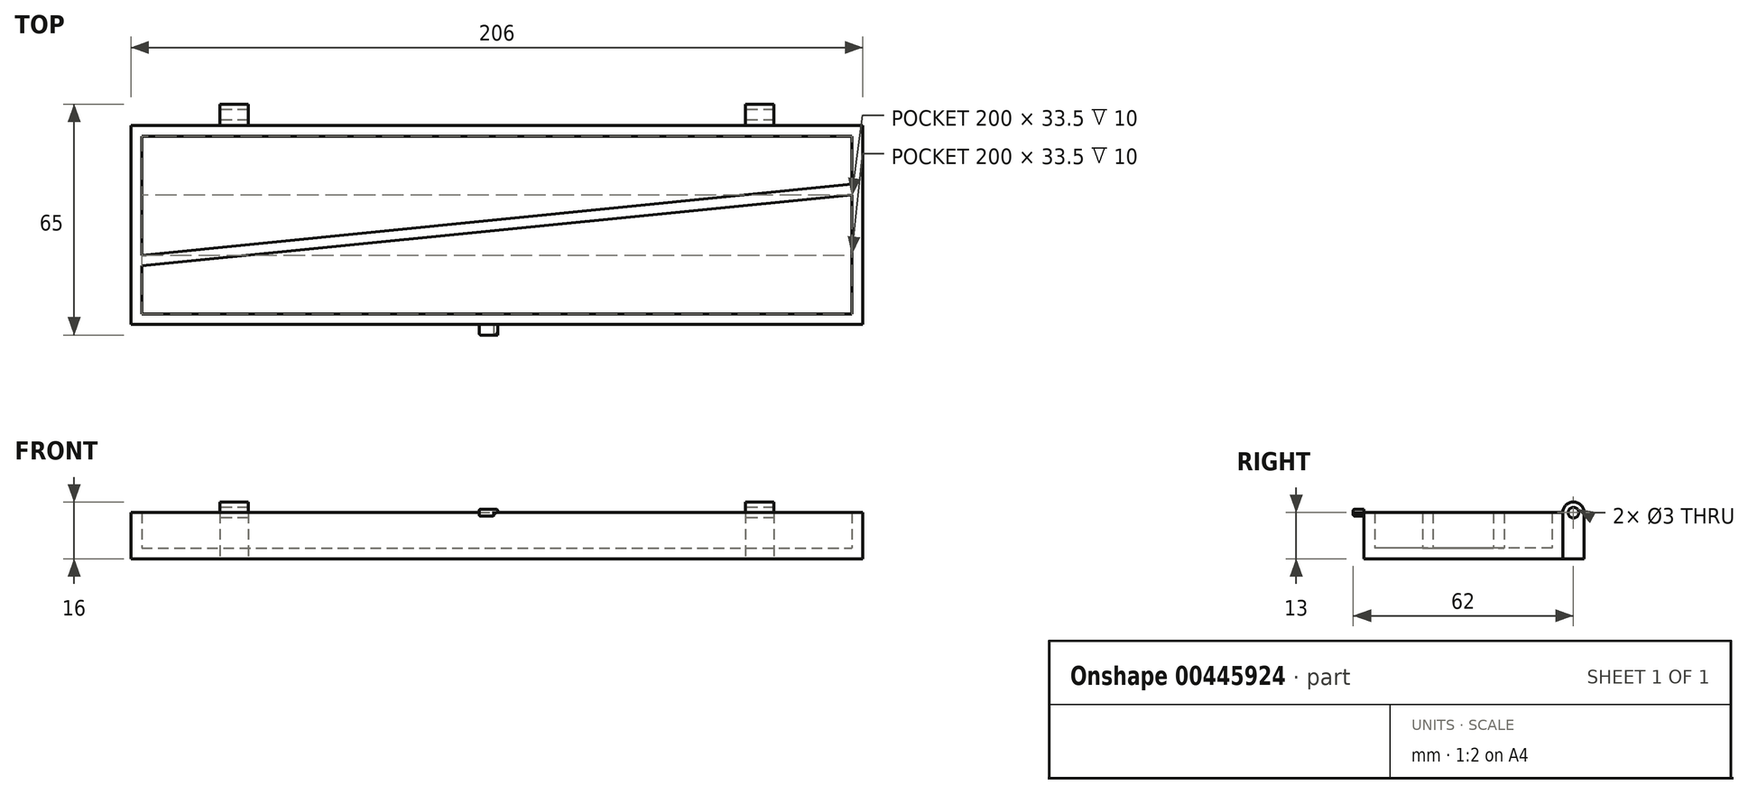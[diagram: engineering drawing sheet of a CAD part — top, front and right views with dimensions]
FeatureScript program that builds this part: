
annotation { "Feature Type Name" : "Feature", "Feature Type Description" : "" }
export const myFeature = defineFeature(function(context is Context, id is Id, definition is map)
    precondition{}
    {
        {
            var Q0;
            Q0=qCreatedBy(makeId("Top.planeOp"),FACE);
            var sketch = newSketch(context, id + "F0", { "sketchPlane" : qUnion([Q0])});
            skLineSegment(sketch, "E0.bottom", {"start": v(-103, 28) * mm, "end": v(103, 28) * mm});
            skLineSegment(sketch, "E0.top", {"start": v(-103, -28) * mm, "end": v(103, -28) * mm});
            skLineSegment(sketch, "E0.left", {"start": v(-103, 28) * mm, "end": v(-103, -28) * mm});
            skLineSegment(sketch, "E0.right", {"start": v(103, 28) * mm, "end": v(103, -28) * mm});
            skSolve(sketch);
        }
        {
            var Q0;
            Q0 = qSketchRegion(id + "F0", true);
            extrude(context, id + "F1", {"entities" : qUnion([Q0]), "depth" : 13 * mm});
        }
        {
            var Q0;
            Q0=makeQuery(id+"F1.opExtrude","CAP_FACE",FACE,{"disambiguationData":[OSD([sQuery(id+"F0.wireOp",EDGE,"E0.bottom"),sQuery(id+"F0.wireOp",EDGE,"E0.top"),sQuery(id+"F0.wireOp",EDGE,"E0.left"),sQuery(id+"F0.wireOp",EDGE,"E0.right")])],"isStart":false});
            shell(context, id + "F2", {"entities" : qUnion([Q0]), "thickness" : 3 * mm});
        }
        {
            var Q0;
            Q0=makeQuery(id+"F2.opShell","OFFSET_FACE",FACE,{"disambiguationData":[OSD([sQuery(id+"F0.wireOp",EDGE,"E0.bottom"),sQuery(id+"F0.wireOp",EDGE,"E0.top"),sQuery(id+"F0.wireOp",EDGE,"E0.left"),sQuery(id+"F0.wireOp",EDGE,"E0.right")])]});
            var sketch = newSketch(context, id + "F3", { "sketchPlane" : qUnion([Q0])});
            skLineSegment(sketch, "E1", {"start": v(-100, -8.5) * mm, "end": v(100, 11.5) * mm});
            skLineSegment(sketch, "E2", {"start": v(-100, -11.5) * mm, "end": v(100, 8.5) * mm});
            skLineSegment(sketch, "E3", {"start": v(-100, -11.5) * mm, "end": v(-100, -8.5) * mm});
            skLineSegment(sketch, "E4", {"start": v(100, 8.5) * mm, "end": v(100, 11.5) * mm});
            skSolve(sketch);
        }
        {
            var Q0;
            Q0 = qSketchRegion(id + "F3", true);
            extrude(context, id + "F4", {"entities" : qUnion([Q0]), "operationType" : NewBodyOperationType.ADD, "depth" : 10 * mm});
        }
        {
            var Q0;
            Q0=makeQuery(id+"F1.opExtrude","SWEPT_FACE",FACE,{"disambiguationData":[OSD([sQuery(id+"F0.wireOp",EDGE,"E0.bottom")])]});
            var sketch = newSketch(context, id + "F5", { "sketchPlane" : qUnion([Q0])});
            skLineSegment(sketch, "E5.bottom", {"start": v(-78, 13) * mm, "end": v(-70, 13) * mm});
            skLineSegment(sketch, "E5.top", {"start": v(-78, 0) * mm, "end": v(-70, 0) * mm});
            skLineSegment(sketch, "E5.left", {"start": v(-78, 13) * mm, "end": v(-78, 0) * mm});
            skLineSegment(sketch, "E5.right", {"start": v(-70, 13) * mm, "end": v(-70, 0) * mm});
            skLineSegment(sketch, "E6.bottom", {"start": v(78, 13) * mm, "end": v(70, 13) * mm});
            skLineSegment(sketch, "E6.top", {"start": v(78, 0) * mm, "end": v(70, 0) * mm});
            skLineSegment(sketch, "E6.left", {"start": v(78, 13) * mm, "end": v(78, 0) * mm});
            skLineSegment(sketch, "E6.right", {"start": v(70, 13) * mm, "end": v(70, 0) * mm});
            skSolve(sketch);
        }
        {
            var Q0;
            Q0 = qSketchRegion(id + "F5", true);
            extrude(context, id + "F6", {"entities" : qUnion([Q0]), "operationType" : NewBodyOperationType.ADD, "depth" : 6 * mm});
        }
        {
            var Q0;
            Q0=makeQuery(id+"F6.boolean.opBoolean","MERGE",FACE,{"derivedFrom":[makeQuery(id+"F4.boolean.opBoolean","MERGE",FACE,{"derivedFrom":[makeQuery(id+"F1.opExtrude","CAP_FACE",FACE,{"disambiguationData":[OSD([sQuery(id+"F0.wireOp",EDGE,"E0.bottom"),sQuery(id+"F0.wireOp",EDGE,"E0.top"),sQuery(id+"F0.wireOp",EDGE,"E0.left"),sQuery(id+"F0.wireOp",EDGE,"E0.right")])],"isStart":false}),makeQuery(id+"F4.opExtrude","CAP_FACE",FACE,{"disambiguationData":[OSD([sQuery(id+"F3.wireOp",EDGE,"E1"),sQuery(id+"F3.wireOp",EDGE,"E2"),sQuery(id+"F3.wireOp",EDGE,"E3"),sQuery(id+"F3.wireOp",EDGE,"E4")])],"isStart":false})]}),makeQuery(id+"F6.opExtrude","SWEPT_FACE",FACE,{"disambiguationData":[OSD([sQuery(id+"F5.wireOp",EDGE,"E5.bottom")])]}),makeQuery(id+"F6.opExtrude","SWEPT_FACE",FACE,{"disambiguationData":[OSD([sQuery(id+"F5.wireOp",EDGE,"E6.bottom")])]})]});
            var sketch = newSketch(context, id + "F7", { "sketchPlane" : qUnion([Q0])});
            skLineSegment(sketch, "E7.bottom", {"start": v(-78, 34) * mm, "end": v(-70, 34) * mm});
            skLineSegment(sketch, "E7.top", {"start": v(-78, 28) * mm, "end": v(-70, 28) * mm});
            skLineSegment(sketch, "E7.left", {"start": v(-78, 34) * mm, "end": v(-78, 28) * mm});
            skLineSegment(sketch, "E7.right", {"start": v(-70, 34) * mm, "end": v(-70, 28) * mm});
            skLineSegment(sketch, "E8.bottom", {"start": v(70, 34) * mm, "end": v(78, 34) * mm});
            skLineSegment(sketch, "E8.top", {"start": v(70, 28) * mm, "end": v(78, 28) * mm});
            skLineSegment(sketch, "E8.left", {"start": v(70, 34) * mm, "end": v(70, 28) * mm});
            skLineSegment(sketch, "E8.right", {"start": v(78, 34) * mm, "end": v(78, 28) * mm});
            skSolve(sketch);
        }
        {
            var Q0;
            Q0 = qSketchRegion(id + "F7", true);
            extrude(context, id + "F8", {"entities" : qUnion([Q0]), "operationType" : NewBodyOperationType.ADD, "depth" : 3 * mm});
        }
        {
            var Q0;
            Q0=makeQuery(id+"F8.opExtrude","CAP_EDGE",EDGE,{"disambiguationData":[OSD([sQuery(id+"F7.wireOp",EDGE,"E7.top")])],"isStart":false});
            var Q1;
            Q1=makeQuery(id+"F8.opExtrude","CAP_EDGE",EDGE,{"disambiguationData":[OSD([sQuery(id+"F7.wireOp",EDGE,"E7.bottom")])],"isStart":false});
            var Q2;
            Q2=makeQuery(id+"F8.opExtrude","CAP_EDGE",EDGE,{"disambiguationData":[OSD([sQuery(id+"F7.wireOp",EDGE,"E8.bottom")])],"isStart":false});
            var Q3;
            Q3=makeQuery(id+"F8.opExtrude","CAP_EDGE",EDGE,{"disambiguationData":[OSD([sQuery(id+"F7.wireOp",EDGE,"E8.top")])],"isStart":false});
            fillet(context, id + "F9", {"entities" : qUnion([Q0, Q1, Q2, Q3]), "radius" : 3 * mm, "tangentPropagation" : true, "allowEdgeOverflow" : false});
        }
        {
            var Q0;
            Q0=makeQuery(id+"F8.boolean.opBoolean","MERGE",FACE,{"derivedFrom":[makeQuery(id+"F6.opExtrude","SWEPT_FACE",FACE,{"disambiguationData":[OSD([sQuery(id+"F5.wireOp",EDGE,"E5.left")])]}),makeQuery(id+"F8.opExtrude","SWEPT_FACE",FACE,{"disambiguationData":[OSD([sQuery(id+"F7.wireOp",EDGE,"E8.right")])]})]});
            var sketch = newSketch(context, id + "F10", { "sketchPlane" : qUnion([Q0])});
            skPoint(sketch, "E9", {"position": v(31, 13) * mm});
            skSolve(sketch);
        }
        {
            var Q0;
            Q0=sQuery(id+"F10.wireOp",VERTEX,"E9");
            var Q1;
            Q1=makeQuery(id+"F1.opExtrude","SWEPT_BODY",BODY,{"disambiguationData":[OSD([sQuery(id+"F0.wireOp",EDGE,"E0.bottom"),sQuery(id+"F0.wireOp",EDGE,"E0.top"),sQuery(id+"F0.wireOp",EDGE,"E0.left"),sQuery(id+"F0.wireOp",EDGE,"E0.right")])]});
            hole(context, id + "F11", {"style" : HoleStyle.SIMPLE, "endStyle" : HoleEndStyle.THROUGH, "holeDiameter" : 3 * mm, "isTappedThrough" : true, "tappedDepth" : 12 * mm, "tapClearance" : 3, "locations" : qUnion([Q0]), "scope" : qUnion([Q1]), "startStyle" : HoleStartStyle.SKETCH});
        }
        {
            var Q0;
            Q0=makeQuery(id+"F1.opExtrude","SWEPT_FACE",FACE,{"disambiguationData":[OSD([sQuery(id+"F0.wireOp",EDGE,"E0.top")])]});
            var sketch = newSketch(context, id + "F12", { "sketchPlane" : qUnion([Q0])});
            skLineSegment(sketch, "E10", {"start": v(0.25, 13) * mm, "end": v(0.25, 14) * mm});
            skLineSegment(sketch, "E11", {"start": v(0.25, 14) * mm, "end": v(-5, 14) * mm});
            skLineSegment(sketch, "E12", {"start": v(-5, 14) * mm, "end": v(-5, 12) * mm});
            skLineSegment(sketch, "E13", {"start": v(0.25, 13) * mm, "end": v(-0.75, 12.92) * mm});
            skLineSegment(sketch, "E14", {"start": v(-0.5, 12) * mm, "end": v(-5, 12) * mm});
            skLineSegment(sketch, "E15", {"start": v(-0.75, 12) * mm, "end": v(-0.75, 12.92) * mm});
            skSolve(sketch);
        }
        {
            var Q0;
            {var subQ1=sQuery(id+"F12.wireOp",EDGE,"E13");Q0=makeQuery(id+"F12.imprint","IMPRINT",FACE,{"disambiguationData":[TD([[makeQuery(id+"F12.imprint","IMPRINT",EDGE,{"derivedFrom":subQ1}),-1.0]])]});}
            var Q1;
            {var subQ0=sQuery(id+"F12.wireOp",EDGE,"E10");Q1=makeQuery(id+"F12.imprint","IMPRINT",FACE,{"disambiguationData":[TD([[makeQuery(id+"F12.imprint","IMPRINT",EDGE,{"derivedFrom":subQ0}),1.0]])]});}
            extrude(context, id + "F13", {"entities" : qUnion([Q0, Q1]), "operationType" : NewBodyOperationType.ADD, "depth" : 3 * mm});
        }
        {
            var Q0;
            Q0=makeQuery(id+"F13.opExtrude","SWEPT_EDGE",EDGE,{"disambiguationData":[OSD([sQuery(id+"F12.wireOp",EDGE,"E10"),sQuery(id+"F12.wireOp",EDGE,"E11")])]});
            var Q1;
            Q1=makeQuery(id+"F13.opExtrude","SWEPT_EDGE",EDGE,{"disambiguationData":[OSD([sQuery(id+"F0.wireOp",EDGE,"E0.top"),sQuery(id+"F12.wireOp",EDGE,"E10"),sQuery(id+"F12.wireOp",EDGE,"E13")])]});
            var Q2;
            Q2=makeQuery(id+"F13.opExtrude","SWEPT_EDGE",EDGE,{"disambiguationData":[OSD([sQuery(id+"F12.wireOp",EDGE,"E11"),sQuery(id+"F12.wireOp",EDGE,"E12")])]});
            var Q3;
            Q3=makeQuery(id+"F13.opExtrude","CAP_EDGE",EDGE,{"disambiguationData":[OSD([sQuery(id+"F12.wireOp",EDGE,"E11")])],"isStart":false});
            var Q4;
            Q4=makeQuery(id+"F13.opExtrude","CAP_EDGE",EDGE,{"disambiguationData":[OSD([sQuery(id+"F12.wireOp",EDGE,"E14")])],"isStart":false});
            var Q5;
            Q5=makeQuery(id+"F13.opExtrude","SWEPT_EDGE",EDGE,{"disambiguationData":[OSD([sQuery(id+"F12.wireOp",EDGE,"E14"),sQuery(id+"F12.wireOp",EDGE,"E15")])]});
            var Q6;
            Q6=makeQuery(id+"F13.opExtrude","SWEPT_EDGE",EDGE,{"disambiguationData":[OSD([sQuery(id+"F12.wireOp",EDGE,"E12"),sQuery(id+"F12.wireOp",EDGE,"E14")])]});
            var Q7;
            Q7=makeQuery(id+"F13.opExtrude","CAP_EDGE",EDGE,{"disambiguationData":[OSD([sQuery(id+"F12.wireOp",EDGE,"E12")])],"isStart":false});
            var Q8;
            Q8=makeQuery(id+"F13.opExtrude","CAP_EDGE",EDGE,{"disambiguationData":[OSD([sQuery(id+"F12.wireOp",EDGE,"E15")])],"isStart":false});
            fillet(context, id + "F14", {"entities" : qUnion([Q0, Q1, Q2, Q3, Q4, Q5, Q6, Q7, Q8]), "radius" : .5 * mm, "tangentPropagation" : true, "allowEdgeOverflow" : false});
        }
    });
